# Revit family: BRITT-0580xxWS8xxR0900
name_source: partatom
category: Oprawy oświetleniowe
units: mm (PartAtom-declared; Revit-internal decimal feet)

## family parameters
Numer OmniClass = 23.80.70.11
Obiekt nadrzędny = Powierzchnia
Punkt obliczania pomieszczeń = Nie
Tnij formami wycięć po wczytaniu = Nie
Typ części = Normalny
Tytuł OmniClass = Luminaries for Internal Lighting
Współdzielony = Nie
Wymiar okrągłego złącza = Użyj średnicy
Źródło światła = Tak

## types (6) — shared parameters
Emituj kształt widoczny w renderingu = Nie
Emituj z długości prostokąta = 186 mm  [stored 0.610236 ft]
Emituj z szerokości prostokąta = 570 mm  [stored 1.87008 ft]
Filtr koloru = 16777215
Kod zespołu = D5020200
Lampa = LED
Obciążenie pozorne = 62 VA
Odchylenie kierunku = 90.00°
Plik sieci fotometrycznej = BRITT 0580DAWS840R0900.IES
Producent = RIDI Leuchten GmbH
URL = www.ridi.de
Zmiana temperatury barwowej przyciemniania lampy = <Brak>
brand = RIDI
conformity mark = CE
electrical safety class = 1
height = 99 mm  [stored 0.324803 ft]
ingress protection (IP) code = IP20
length = 579 mm
nominal frequency = 50-60Hz
nominal voltage = 230
rated input power = 62
voltage type (AC, DC, UC) = AC
weight = 3,39
width = 190 mm
zero-valued in all types: Domyślna rzędna

## per-type parameters (varying)
| type | Model |
| BRITT 0580NDWS830R0900 | 0326693 |
| BRITT 0580DAWS830R0900 | 0336693 |
| BRITT 0580NDWS835R0900 | 0326694 |
| BRITT 0580DAWS835R0900 | 0336694 |
| BRITT 0580NDWS840R0900 | 0326695 |
| BRITT 0580DAWS840R0900 | 0336695 |

note: column(s) folded — value = type name in every type: product name

note: [stored X ft] marks values corroborated as IEEE doubles in the binary element streams (Revit-internal decimal feet)
